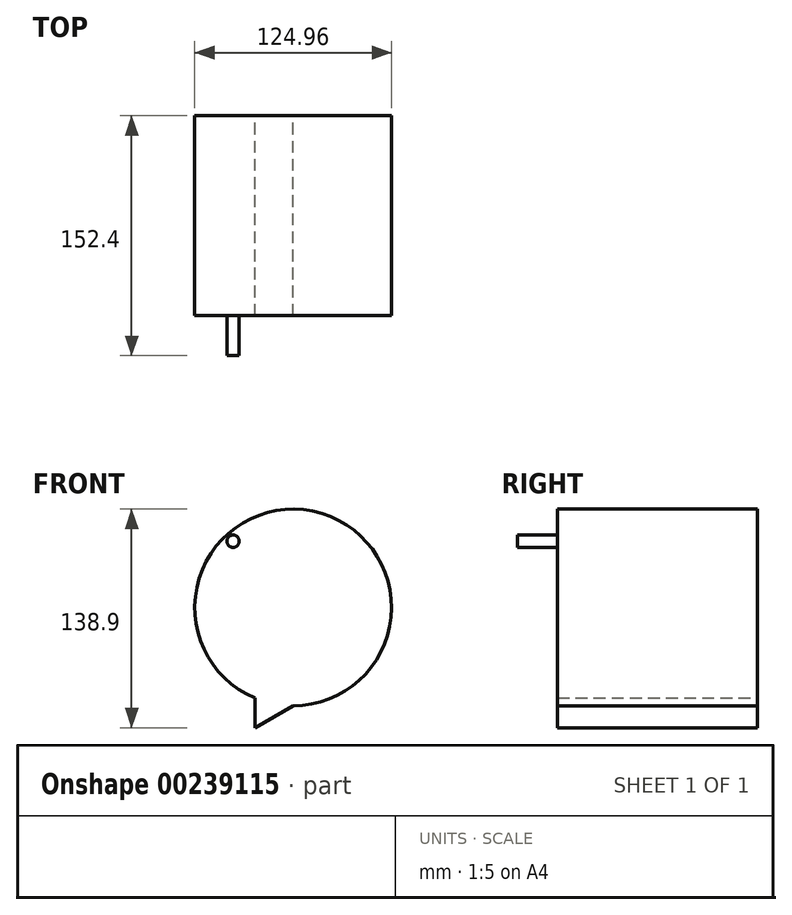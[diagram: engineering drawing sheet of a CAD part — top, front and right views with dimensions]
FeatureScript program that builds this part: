
annotation { "Feature Type Name" : "Feature", "Feature Type Description" : "" }
export const myFeature = defineFeature(function(context is Context, id is Id, definition is map)
    precondition{}
    {
        {
            var Q0;
            Q0=qCreatedBy(makeId("Front.planeOp"),FACE);
            var sketch = newSketch(context, id + "F0", { "sketchPlane" : qUnion([Q0])});
            skCircle(sketch, "E0", {"center": v(0, 0) * mm, "radius": 62.48 * mm});
            skSolve(sketch);
        }
        {
            var Q0;
            Q0 = qSketchRegion(id + "F0", true);
            extrude(context, id + "F1", {"entities" : qUnion([Q0]), "endBound" : BoundingType.SYMMETRIC, "depth" : 127 * mm});
        }
        {
            var Q0;
            Q0=makeQuery(id+"F1.opExtrude","CAP_FACE",FACE,{"disambiguationData":[OSD([sQuery(id+"F0.wireOp",EDGE,"E0")])],"isStart":false});
            var sketch = newSketch(context, id + "F2", { "sketchPlane" : qUnion([Q0])});
            skCircle(sketch, "E1", {"center": v(-38.17, 42.1) * mm, "radius": 3.93 * mm});
            skSolve(sketch);
        }
        {
            var Q0;
            Q0 = qSketchRegion(id + "F2", true);
            extrude(context, id + "F3", {"entities" : qUnion([Q0]), "operationType" : NewBodyOperationType.ADD, "depth" : 25.4 * mm});
        }
        {
            var Q0;
            Q0=makeQuery(id+"F1.opExtrude","CAP_FACE",FACE,{"disambiguationData":[OSD([sQuery(id+"F0.wireOp",EDGE,"E0")])],"isStart":true});
            var sketch = newSketch(context, id + "F4", { "sketchPlane" : qUnion([Q0])});
            skLineSegment(sketch, "E2", {"start": v(24.34, -57.55) * mm, "end": v(24.34, -76.42) * mm});
            skLineSegment(sketch, "E3", {"start": v(24.34, -76.42) * mm, "end": v(0, -62.48) * mm});
            skLineSegment(sketch, "E4", {"start": v(0, -62.48) * mm, "end": v(24.34, -57.55) * mm});
            skSolve(sketch);
        }
        {
            var Q0;
            Q0 = qSketchRegion(id + "F4", true);
            extrude(context, id + "F5", {"entities" : qUnion([Q0]), "operationType" : NewBodyOperationType.ADD, "oppositeDirection" : true, "depth" : 127 * mm});
        }
    });
